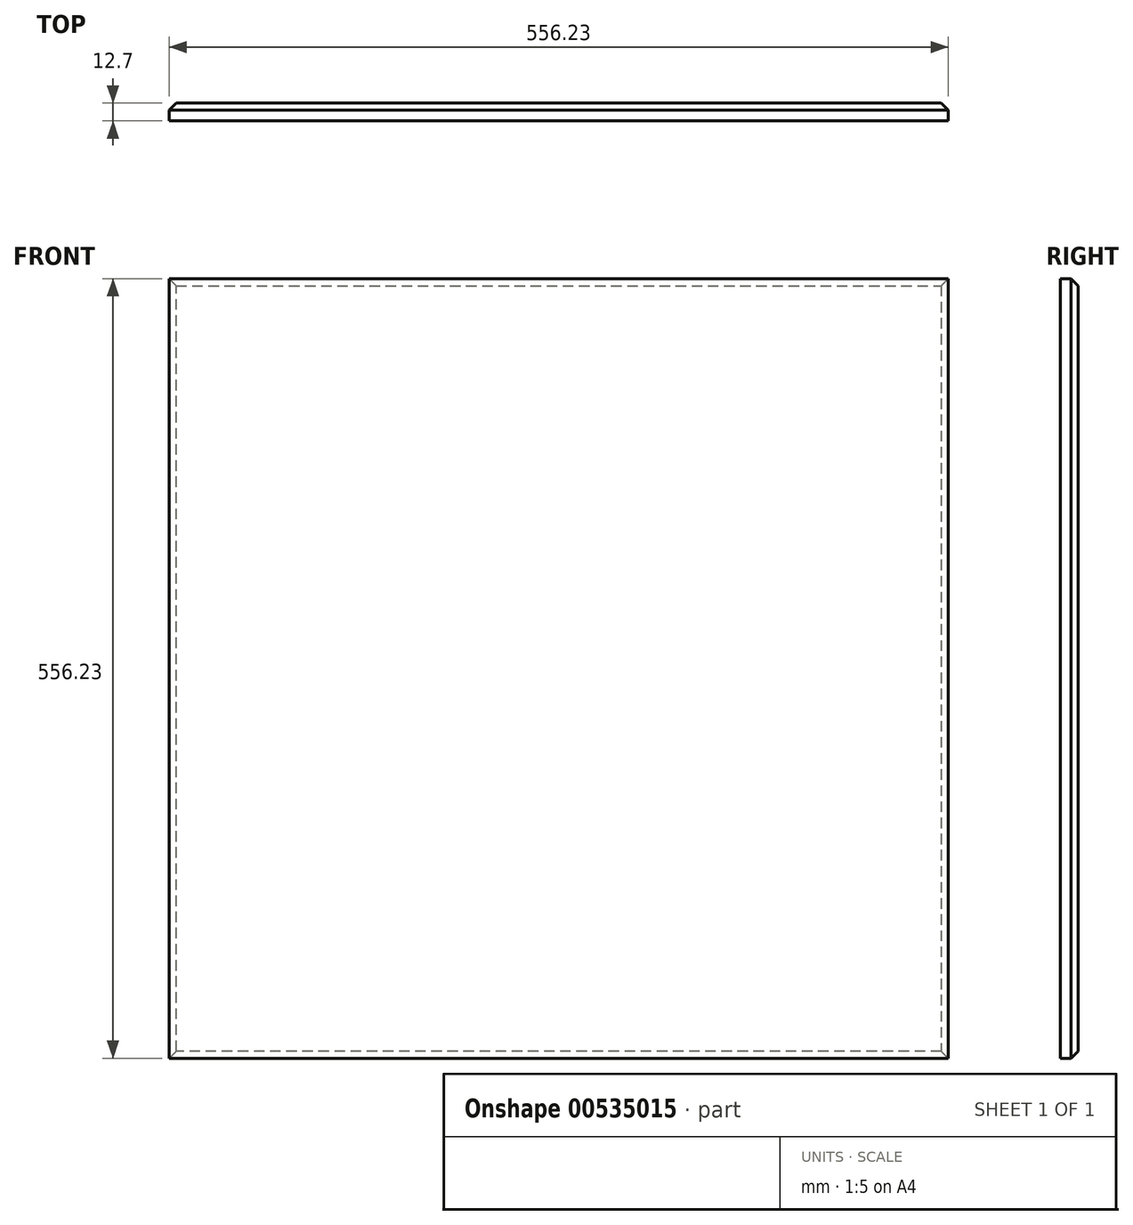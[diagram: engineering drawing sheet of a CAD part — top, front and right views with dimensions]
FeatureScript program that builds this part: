
annotation { "Feature Type Name" : "Feature", "Feature Type Description" : "" }
export const myFeature = defineFeature(function(context is Context, id is Id, definition is map)
    precondition{}
    {
        {
            var Q0;
            Q0=qCreatedBy(makeId("Front.planeOp"),FACE);
            var sketch = newSketch(context, id + "F0", { "sketchPlane" : qUnion([Q0])});
            skLineSegment(sketch, "E0.bottom", {"start": v(-267.34, 317.15) * mm, "end": v(288.9, 317.15) * mm});
            skLineSegment(sketch, "E0.top", {"start": v(-267.34, -239.08) * mm, "end": v(288.9, -239.08) * mm});
            skLineSegment(sketch, "E0.left", {"start": v(-267.34, 317.15) * mm, "end": v(-267.34, -239.08) * mm});
            skLineSegment(sketch, "E0.right", {"start": v(288.9, 317.15) * mm, "end": v(288.9, -239.08) * mm});
            skSolve(sketch);
        }
        {
            var Q0;
            Q0=makeQuery(id+"F0.imprint","IMPRINT",FACE,{"disambiguationData":[TD([[makeQuery(id+"F0.imprint","IMPRINT",EDGE,{"derivedFrom":sQuery(id+"F0.wireOp",EDGE,"E0.bottom")}),-1.0]])]});
            extrude(context, id + "F1", {"entities" : qUnion([Q0]), "depth" : 12.7 * mm, "offsetDistance" : 25.4 * mm});
        }
        {
            var Q0;
            Q0=makeQuery(id+"F1.opExtrude","CAP_EDGE",EDGE,{"disambiguationData":[OSD([sQuery(id+"F0.wireOp",EDGE,"E0.bottom")])],"isStart":true});
            chamfer(context, id + "F2", {"entities" : qUnion([Q0]), "width" : 5.08 * mm, "tangentPropagation" : true});
        }
        {
            var Q0;
            Q0=makeQuery(id+"F1.opExtrude","CAP_EDGE",EDGE,{"disambiguationData":[OSD([sQuery(id+"F0.wireOp",EDGE,"E0.right")])],"isStart":true});
            chamfer(context, id + "F3", {"entities" : qUnion([Q0]), "width" : 5.08 * mm, "tangentPropagation" : true});
        }
        {
            var Q0;
            Q0=makeQuery(id+"F1.opExtrude","CAP_EDGE",EDGE,{"disambiguationData":[OSD([sQuery(id+"F0.wireOp",EDGE,"E0.top")])],"isStart":true});
            chamfer(context, id + "F4", {"entities" : qUnion([Q0]), "width" : 5.08 * mm, "tangentPropagation" : true});
        }
        {
            var Q0;
            Q0=makeQuery(id+"F1.opExtrude","CAP_EDGE",EDGE,{"disambiguationData":[OSD([sQuery(id+"F0.wireOp",EDGE,"E0.left")])],"isStart":true});
            chamfer(context, id + "F5", {"entities" : qUnion([Q0]), "width" : 5.08 * mm, "tangentPropagation" : true});
        }
    });
